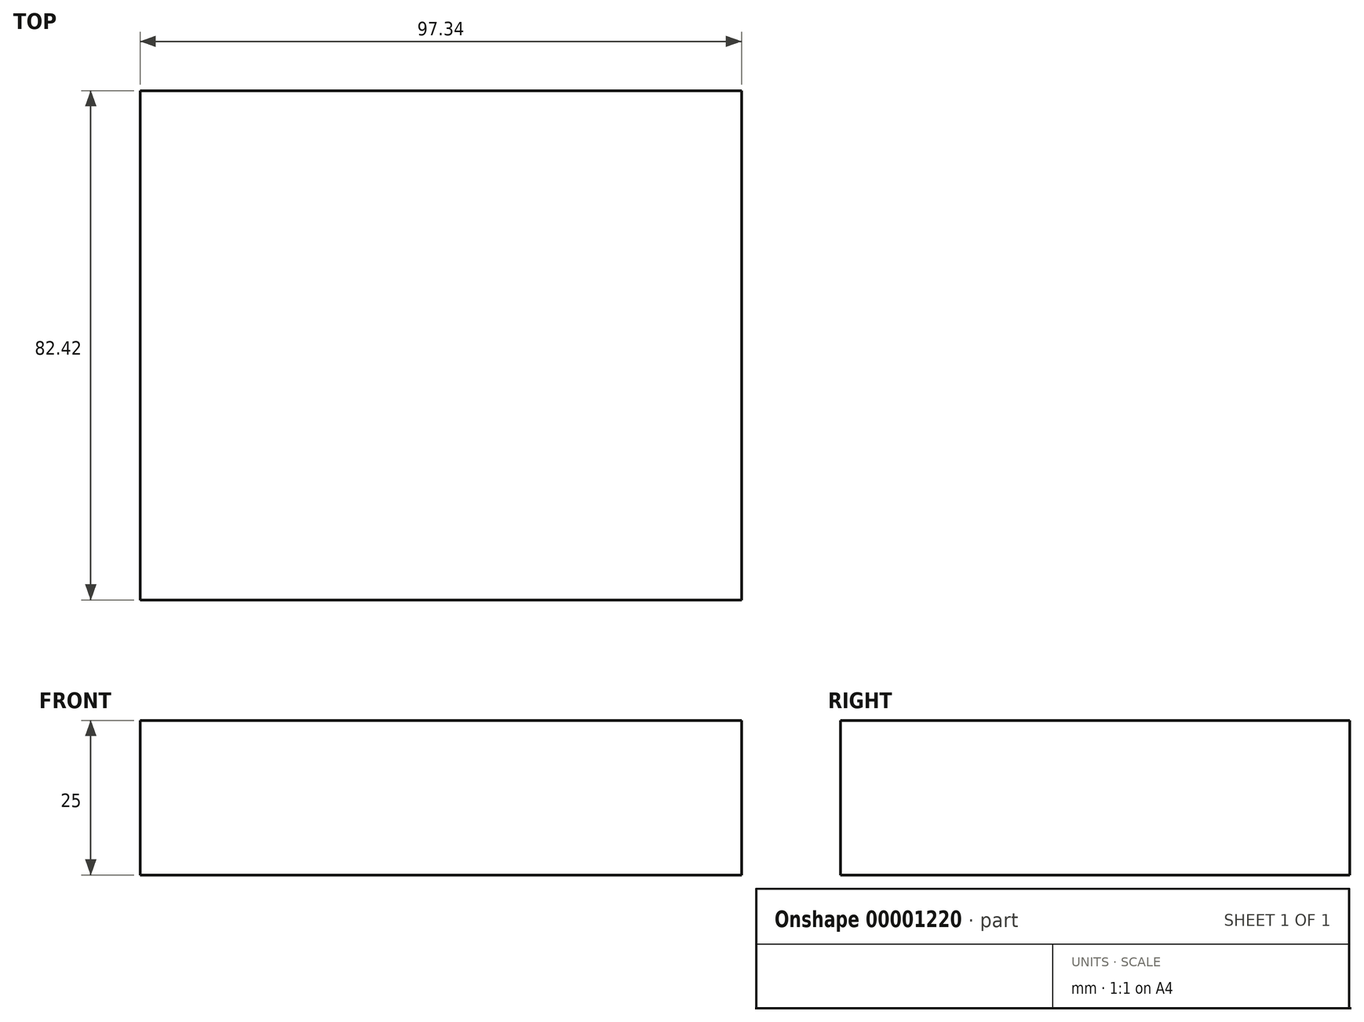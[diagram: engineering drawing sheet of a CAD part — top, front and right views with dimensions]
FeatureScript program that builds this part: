
annotation { "Feature Type Name" : "Feature", "Feature Type Description" : "" }
export const myFeature = defineFeature(function(context is Context, id is Id, definition is map)
    precondition{}
    {
        {
            var Q0;
            Q0=qCreatedBy(makeId("Top.planeOp"),FACE);
            var sketch = newSketch(context, id + "F0", { "sketchPlane" : qUnion([Q0])});
            skLineSegment(sketch, "E0.bottom", {"start": v(-92.93, 55.46) * mm, "end": v(4.41, 55.46) * mm});
            skLineSegment(sketch, "E0.top", {"start": v(-92.93, -26.96) * mm, "end": v(4.41, -26.96) * mm});
            skLineSegment(sketch, "E0.left", {"start": v(-92.93, 55.46) * mm, "end": v(-92.93, -26.96) * mm});
            skLineSegment(sketch, "E0.right", {"start": v(4.41, 55.46) * mm, "end": v(4.41, -26.96) * mm});
            skSolve(sketch);
        }
        {
            var Q0;
            Q0=makeQuery(id+"F0.imprint","IMPRINT",FACE,{"disambiguationData":[TD([[makeQuery(id+"F0.imprint","IMPRINT",EDGE,{"derivedFrom":sQuery(id+"F0.wireOp",EDGE,"E0.bottom")}),-1.0]])]});
            extrude(context, id + "F1", {"entities" : qUnion([Q0]), "depth" : 25 * mm, "offsetDistance" : 25 * mm});
        }
    });
